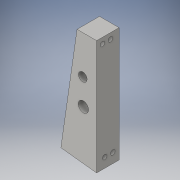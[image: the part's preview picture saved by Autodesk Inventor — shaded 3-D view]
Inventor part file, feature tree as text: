
AUTODESK INVENTOR PART (.ipt)
format: ipt  version: 2016 (Build 200138000, 138)  size: 128,000 bytes
history: native  units: in
note: dims shown in document units (in); Inventor stores cm internally (conversion verified against a paired STEP export)
features: extrude x3, sketch x3
ambient origin geometry x8: Origin, YZ Plane, XZ Plane, XY Plane, X Axis, Y Axis, Z Axis, Center Point
bodies: Solid1 (feature_tree)
feature tree (6):
  extrude  "Extrusion1"  Depth=2.4409in
  extrude  "Extrusion2"  Depth=0.2756in
  extrude  "Extrusion3"  Depth=1.5354in
  sketch  "Sketch1"  dims[d0=7.8346in d1=2.4409in]
  sketch  "Sketch2"  dims[d2=1.3386in d3=0.2756in]
  sketch  "Sketch3"  dims[d4=1.5354in d5=0.0in d6=0.315in d7=0.315in d8=0.5512in d9=0.5512in d10=6.7717in d11=0.315in d12=0.315in d13=0.5512in d14=0.3937in d16=1.5354in d17=0.0in d18=0.3937in d19=0.7087in d20=0.5906in d21=0.9055in d22=0.9449in d23=2.6181in d24=4.3701in d25=1.5354in d26=0.0in]
